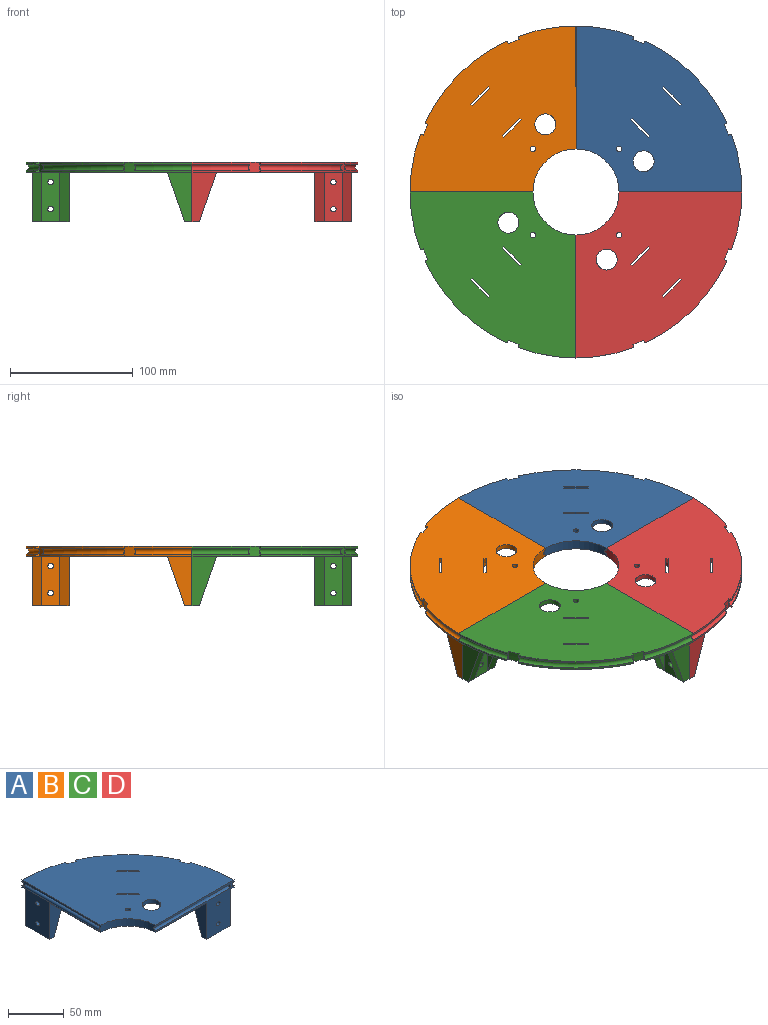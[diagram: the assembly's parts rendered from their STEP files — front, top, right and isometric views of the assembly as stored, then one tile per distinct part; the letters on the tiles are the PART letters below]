
ASSEMBLY  parts=4 mates=9
PART A: 74 faces, bbox 141x139x48 mm
  f0: plane 135x135mm, normal (0,0,-1), area 2344.3mm2, adj f12,f13,f21,f23,f25,f27,f29,f31
  f1: plane 4x1.41mm, normal (0.71,-0.71,0), area 8mm2, adj f2,f4,f10,f59
  f2: plane 14.14x14.14mm, normal (-0.71,-0.71,0), area 80mm2, adj f1,f3,f10,f59
  f3: plane 4x1.41mm, normal (-0.71,0.71,0), area 8mm2, adj f2,f4,f10,f59
  f4: plane 14.14x14.14mm, normal (0.71,0.71,0), area 80mm2, adj f1,f3,f10,f59
  f5: plane 14.14x14.14mm, normal (0.71,0.71,0), area 80mm2, adj f6,f8,f10,f59
  f6: plane 4x1.41mm, normal (0.71,-0.71,0), area 8mm2, adj f5,f7,f10,f59
  f7: plane 14.14x14.14mm, normal (-0.71,-0.71,0), area 80mm2, adj f6,f8,f10,f59
  f8: plane 4x1.41mm, normal (-0.71,0.71,0), area 8mm2, adj f5,f7,f10,f59
  f9: cylinder r=8.5mm len=17mm, axis (0,0,-1), area 213.6mm2, adj f10,f59
  f10: plane 135x135mm, normal (0,0,1), area 12979.3mm2, adj f1,f2,f3,f4,f5,f6,f7,f8
  f11: plane 100x100mm, normal (0,0,-1), area 1601.5mm2, adj f22,f23,f24,f25,f28,f30,f63,f64
  f12: cylinder r=135mm len=66.48mm, axis (0,0,-1), area 144mm2, adj f0,f16,f46,f50
  f13: cylinder r=135mm len=47mm, axis (0,0,-1), area 72mm2, adj f0,f17,f25,f48
  f14: cylinder r=135mm len=66.48mm, axis (0,0,-1), area 144mm2, adj f10,f16,f47,f51
  f15: cylinder r=135mm len=47mm, axis (0,0,-1), area 72mm2, adj f10,f17,f25,f49
  f16: torus R=135mm, axis (0,0,1), area 745.3mm2, adj f12,f14,f46,f47,f50,f51
  f17: torus R=135mm, axis (0,0,1), area 372.6mm2, adj f13,f15,f25,f48,f49
  f18: plane 30x6mm, normal (0,0,-1), area 180mm2, adj f23,f27,f28,f35,f37,f38
  f19: plane 30x6mm, normal (0,0,-1), area 180mm2, adj f25,f29,f30,f33,f41,f42
  f20: cylinder r=135mm len=47.01mm, axis (0,0,-1), area 72mm2, adj f10,f23,f26,f54
  f21: cylinder r=135mm len=47.01mm, axis (0,0,-1), area 72mm2, adj f0,f23,f26,f53
  f22: cylinder r=35mm len=37mm, axis (0,0,-1), area 439.2mm2, adj f10,f11,f23,f25,f56,f58
  f23: plane 100x48mm, normal (0,-1,0), area 1558.5mm2, adj f0,f10,f11,f18,f20,f21,f22,f26
  f24: cylinder r=2.25mm len=8mm, axis (0,0,-1), area 113.1mm2, adj f10,f11
  f25: plane 100x48mm, normal (-1,0,0), area 1578.4mm2, adj f0,f10,f11,f13,f15,f17,f19,f22
  f26: torus R=135mm, axis (0,0,1), area 372.7mm2, adj f20,f21,f23,f53,f54
  f27: plane 40x20mm, normal (1,0,0), area 520mm2, adj f0,f18,f23,f37
  f28: plane 44x20mm, normal (-1,0,0), area 548mm2, adj f11,f18,f23,f38,f59,f62,f72
  f29: plane 40x20mm, normal (0,1,0), area 520mm2, adj f0,f19,f25,f41
  f30: plane 44x20mm, normal (0,-1,0), area 548mm2, adj f11,f19,f25,f42,f59,f60,f73
  f31: plane 40x14mm, normal (0,-1,0), area 280mm2, adj f0,f33,f41
  f32: plane 40x14mm, normal (0,1,0), area 280mm2, adj f0,f33,f42
  f33: plane 40x15mm, normal (1,0,0), area 568.2mm2, adj f0,f19,f31,f32,f43,f44
  f34: plane 40x14mm, normal (-1,0,0), area 280mm2, adj f0,f35,f37
  f35: plane 40x15mm, normal (0,1,0), area 568.2mm2, adj f0,f18,f34,f36,f39,f40
  f36: plane 40x14mm, normal (1,0,0), area 280mm2, adj f0,f35,f38
  f37: plane 40x14mm, normal (0,0.94,-0.33), area 317.8mm2, adj f0,f18,f27,f34
  f38: plane 40x14mm, normal (0,0.94,-0.33), area 317.8mm2, adj f18,f28,f36,f62
  f39: cylinder r=2.25mm len=6mm, axis (0,1,0), area 84.8mm2, adj f23,f35
  f40: cylinder r=2.25mm len=6mm, axis (0,1,0), area 84.8mm2, adj f23,f35
  f41: plane 40x14mm, normal (0.94,0,-0.33), area 317.8mm2, adj f0,f19,f29,f31
  f42: plane 40x14mm, normal (0.94,0,-0.33), area 317.8mm2, adj f19,f30,f32,f60
  f43: cylinder r=2.25mm len=6mm, axis (1,0,0), area 84.8mm2, adj f25,f33
  f44: cylinder r=2.25mm len=6mm, axis (1,0,0), area 84.8mm2, adj f25,f33
  f45: cylinder r=132.5mm len=9.07mm, axis (0,0,1), area 78.5mm2, adj f0,f10,f46,f47,f48,f49
  f46: plane 4x2.27mm, normal (-0.91,0.42,0), area 5.1mm2, adj f0,f12,f16,f45
  f47: plane 4x2.27mm, normal (-0.91,0.42,0), area 5.1mm2, adj f10,f14,f16,f45
  f48: plane 4x2.34mm, normal (0.94,-0.35,0), area 5.1mm2, adj f0,f13,f17,f45
  f49: plane 4x2.34mm, normal (0.94,-0.35,0), area 5.1mm2, adj f10,f15,f17,f45
  f50: plane 4x2.27mm, normal (0.42,-0.91,0), area 5.1mm2, adj f0,f12,f16,f52
  f51: plane 4x2.27mm, normal (0.42,-0.91,0), area 5.1mm2, adj f10,f14,f16,f52
  f52: cylinder r=132.5mm len=9.07mm, axis (0,0,1), area 78.5mm2, adj f0,f10,f50,f51,f53,f54
  f53: plane 4x2.34mm, normal (-0.35,0.94,0), area 5.1mm2, adj f0,f21,f26,f52
  f54: plane 4x2.34mm, normal (-0.35,0.94,0), area 5.1mm2, adj f10,f20,f26,f52
  f55: plane 4x2mm, normal (0,1,0), area 6.3mm2, adj f25,f56
  f56: cylinder r=2mm len=95.06mm, axis (0,1,0), area 597.1mm2, adj f22,f25,f55
  f57: plane 4.2x2.1mm, normal (-1,0,0), area 6.9mm2, adj f23,f58
  f58: cylinder r=2.1mm len=95.26mm, axis (1,0,0), area 628.3mm2, adj f22,f23,f57
  f59: plane 113.47x113.47mm, normal (0,0,-1), area 8253.5mm2, adj f1,f2,f3,f4,f5,f6,f7,f8
  f60: plane 16.47x4mm, normal (1,0,0), area 65.9mm2, adj f0,f30,f42,f59,f70
  f61: cylinder r=124.12mm len=95.31mm, axis (0,0,-1), area 569.9mm2, adj f0,f59,f70,f71
  f62: plane 16.47x4mm, normal (0,1,0), area 65.9mm2, adj f0,f28,f38,f59,f71
  f63: plane 50x4mm, normal (0,1,0), area 200mm2, adj f11,f59,f64,f72
  f64: cylinder r=5mm len=5mm, axis (0,0,-1), area 31.4mm2, adj f11,f59,f63,f65
  f65: plane 24x4mm, normal (1,0,0), area 96mm2, adj f11,f59,f64,f66
  f66: cylinder r=3mm len=4mm, axis (0,0,-1), area 18.8mm2, adj f11,f59,f65,f67
  f67: plane 24x4mm, normal (0,1,0), area 96mm2, adj f11,f59,f66,f68
  f68: cylinder r=5mm len=5mm, axis (0,0,-1), area 31.4mm2, adj f11,f59,f67,f69
  f69: plane 50x4mm, normal (1,0,0), area 200mm2, adj f11,f59,f68,f73
  f70: cylinder r=5mm len=6.05mm, axis (0,0,-1), area 35.6mm2, adj f0,f59,f60,f61
  f71: cylinder r=5mm len=6.05mm, axis (0,0,-1), area 35.6mm2, adj f0,f59,f61,f62
  f72: cylinder r=5mm len=5mm, axis (0,0,-1), area 31.4mm2, adj f11,f28,f59,f63
  f73: cylinder r=5mm len=5mm, axis (0,0,-1), area 31.4mm2, adj f11,f30,f59,f69
PART B: same geometry as A
PART C: same geometry as A
PART D: same geometry as A
PLACE A t=(6,0,0)mm
PLACE B rot(axis=(0,0,1),90deg) t=(6,0,0)mm
PLACE C rot(axis=(0,0,1),180deg) t=(6,0,0)mm
PLACE D rot(axis=(0,0,-1),90deg) t=(6,0,0)mm
MATE planar C.f40 <-> A.f23  axis (0,1,0) through (-109,0,-8)mm
MATE planar B.f23 <-> A.f43  axis (1,0,0) through (6,107.79,-14.01)mm
MATE planar B.f0 <-> A.f0  axis (0,0,-1) through (-74.55,80.55,0)mm
MATE cylindrical C.f40 <-> B.f43  axis (0,1,0) through (-109,0,-8)mm
MATE cylindrical B.f40 <-> A.f43  axis (1,0,0) through (6,115,-8)mm
MATE planar D.f40 <-> C.f25  axis (-1,0,0) through (6,-115,-8)mm
MATE planar D.f44 <-> A.f39  axis (0,1,0) through (121,0,-30)mm
MATE planar C.f0 <-> A.f0  axis (0,0,-1) through (-74.55,-80.55,0)mm
MATE planar D.f10 <-> C.f10  axis (0,0,1) through (66.87,-60.35,8)mm
